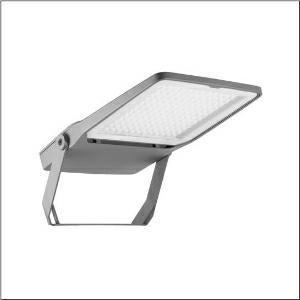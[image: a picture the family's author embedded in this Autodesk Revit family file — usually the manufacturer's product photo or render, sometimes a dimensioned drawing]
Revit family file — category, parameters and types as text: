
# Revit family: floodlight_fl_20_midi___pl61_5xa7682e2c1ac_2141
name_source: partatom
category: Lighting Fixtures
units: mm (PartAtom-declared; Revit-internal decimal feet)

## family parameters
Cut with Voids When Loaded = No
Host = Face
Light Source = No
Part Type = Normal
Room Calculation Point = No
Round Connector Dimension = Use Diameter
Shared = No

## types (1)
- --- (1 x LED 4000K / CRI = 70 (unbekannt), 27150 lm, 4000K)
    Apparent Load = 208 VA
    CIE Flux Codes = 33 65 98 100 100
    Color Rendering = 70
    Color Temperature = 4000K
    Default Elevation = 1800 mm
    Description = Floodlight FL 20 midi, floodlight, primary light control with lens, of plastic, primary optical cover: protective disc, of toughened safety glass, transparent, light distribution: PL61, light emission: direct distribution, primary light characteristic: asymmetric, installation type: surface-mounted, LED High Power LED, rated luminous flux: 27.150 lm, light colour: 740, colour temperature: 4000K, control gear: ECG Plus, control: flexible luminous flux parameterisation, time-dependent luminous flux control, digital communication interface, power reduction, overheat protection, electronic power reduction, with terminal, 5-pole, max. 2.5mm², mains connection: 220..240V, AC, 50/60Hz, rated input power: 208W, LED unit, of diecast aluminium, powder-coated, Siteco® metallic grey (DB 702S), length: 654 mm, width: 450 mm, height: 76mm, housing frame, of diecast aluminium, powder-coated, Siteco® metallic grey (DB 702S), mounting bracket, of steel, powder-coated, Siteco® metallic grey (DB 702S), DALIprotection rating (complete): IP66, insulation class (complete): insulation class II (safety insulation), certification: CE, ENEC, VDE, protection symbol: D, permissible ambient temperature for indoor applications: -40..+40°C, permissible ambient temperature for outdoor applications: -40..+50°C, standard: DIN EN 12944, packaging unit: 1 piece

Light Distribution: PL61
    Height = 76 mm
    Lamp = 1 x LED 4000K / CRI >= 70 (unbekannt)
    Lamp Light Flux = 27150 lm
    Lamp count = 1
    Length = 672 mm
    Luminous efficacy = 131 lm/W
    Manufacturer = Siteco
    ModVariant = No
    Model = 5XA7682E2C1AC
    Number of Poles = 1
    OnlyDefault = Yes
    Power Factor = 1
    Product Name = Floodlight FL 20 midi | PL61
    Product group = floodlight | pylon top
    ProductGroupID = 6101
    Protection Class = Protection class II
    Protection Degree = IP 66
    RLX_Detail_Level = 1
    RlxData = <blob elided: 97945 chars, md5=848dc65a>
    Socket = socket
    Standby Power = 0 W
    System Light Flux = 27150 lm
    System Power = 208 W
    Type Comments = factory setting: luminous flux: 100 % | dim-lin: 254 | 484 mA
    Type Image = l_1005943.jpg
    URL = http://relux.com
    VarID = @adj_142317
    Voltage = 0 V
    Weight = 0.00 kg
    Width = 450 mm

## geometry (parser evidence)
native form markers: Blend x4, Sweep x12
no freeform markers — native parametric forms only
